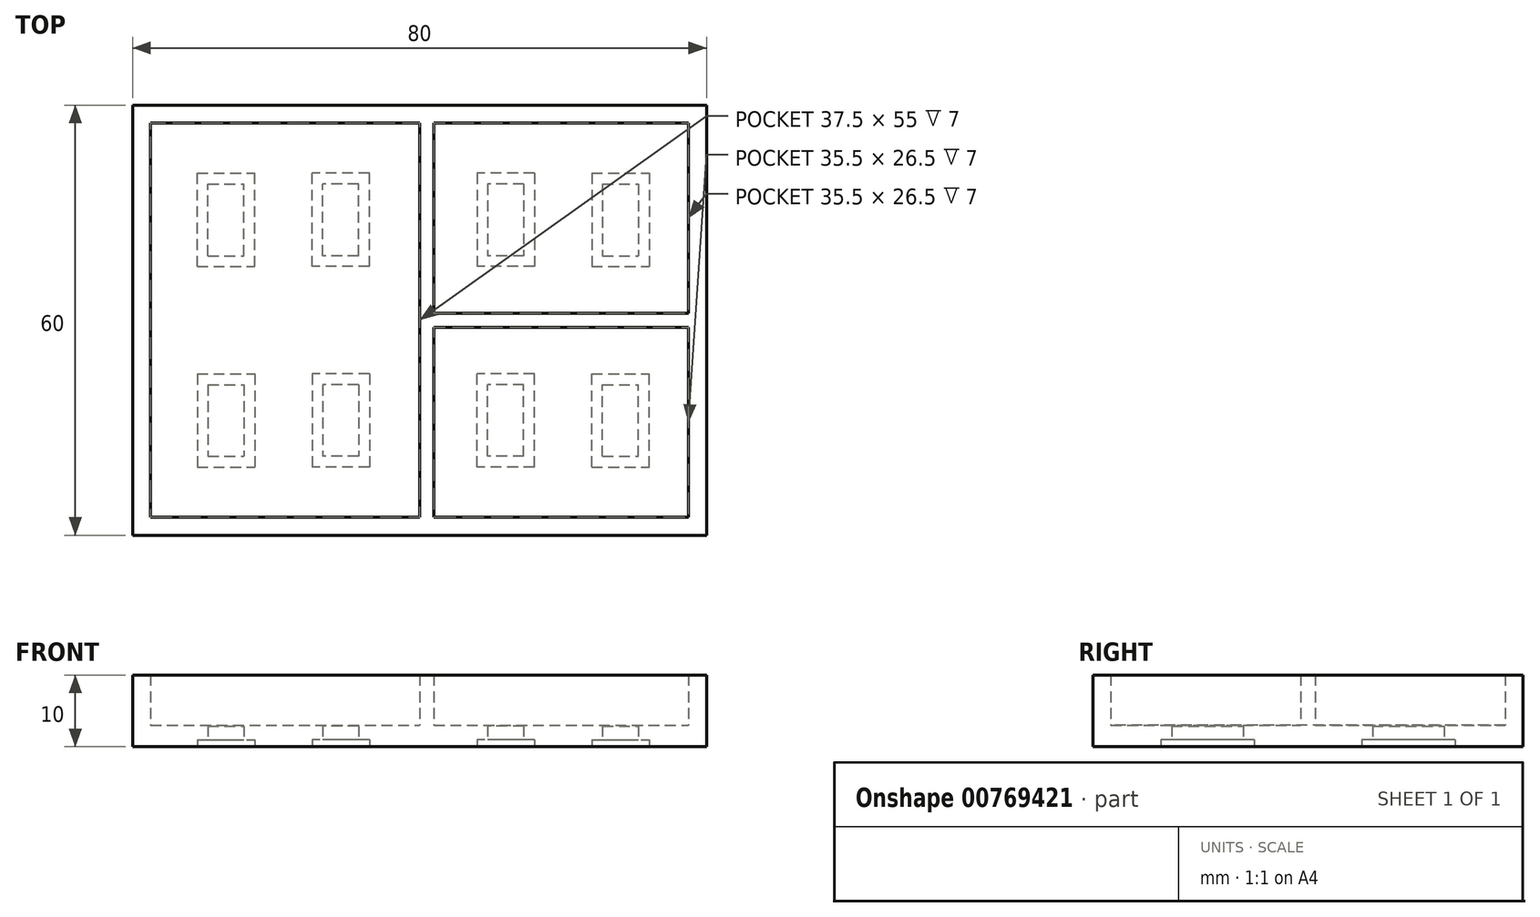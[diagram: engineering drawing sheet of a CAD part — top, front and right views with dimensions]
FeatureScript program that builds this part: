
annotation { "Feature Type Name" : "Feature", "Feature Type Description" : "" }
export const myFeature = defineFeature(function(context is Context, id is Id, definition is map)
    precondition{}
    {
        {
            var Q0;
            Q0=qCreatedBy(makeId("Top.planeOp"),FACE);
            var sketch = newSketch(context, id + "F0", { "sketchPlane" : qUnion([Q0])});
            skLineSegment(sketch, "E0.bottom", {"start": v(0, 0) * mm, "end": v(80, 0) * mm});
            skLineSegment(sketch, "E0.top", {"start": v(0, 60) * mm, "end": v(80, 60) * mm});
            skLineSegment(sketch, "E0.left", {"start": v(0, 0) * mm, "end": v(0, 60) * mm});
            skLineSegment(sketch, "E0.right", {"start": v(80, 0) * mm, "end": v(80, 60) * mm});
            skLineSegment(sketch, "E1", {"start": v(40, 57.5) * mm, "end": v(40, 2.5) * mm});
            skLineSegment(sketch, "E2.0", {"start": v(42, 29) * mm, "end": v(77.5, 29) * mm});
            skLineSegment(sketch, "E3.0", {"start": v(42, 31) * mm, "end": v(77.5, 31) * mm});
            skPoint(sketch, "E4.orphan", {"position": v(80, 30) * mm});
            skPoint(sketch, "E5.start.orphan", {"position": v(40, 30) * mm});
            skLineSegment(sketch, "E6.0", {"start": v(2.5, 2.5) * mm, "end": v(2.5, 57.5) * mm});
            skLineSegment(sketch, "E6.1", {"start": v(2.5, 2.5) * mm, "end": v(40, 2.5) * mm});
            skLineSegment(sketch, "E6.2", {"start": v(77.5, 2.5) * mm, "end": v(77.5, 29) * mm});
            skLineSegment(sketch, "E6.3", {"start": v(2.5, 57.5) * mm, "end": v(40, 57.5) * mm});
            skLineSegment(sketch, "E7", {"start": v(42, 2.5) * mm, "end": v(42, 29) * mm});
            skLineSegment(sketch, "E8.trimOffspring", {"start": v(42, 31) * mm, "end": v(42, 57.5) * mm});
            skLineSegment(sketch, "E9.trimOffspring", {"start": v(77.5, 31) * mm, "end": v(77.5, 57.5) * mm});
            skLineSegment(sketch, "E10.trimOffspring", {"start": v(42, 2.5) * mm, "end": v(77.5, 2.5) * mm});
            skPoint(sketch, "E11.orphan", {"position": v(40, 0) * mm});
            skLineSegment(sketch, "E12.trimOffspring", {"start": v(42, 57.5) * mm, "end": v(77.5, 57.5) * mm});
            skPoint(sketch, "E13.orphan", {"position": v(40, 60) * mm});
            skLineSegment(sketch, "E14", {"start": v(21, 0) * mm, "end": v(21, 60) * mm, "construction": true});
            skLineSegment(sketch, "E15", {"start": v(0, 44) * mm, "end": v(80, 44) * mm, "construction": true});
            skLineSegment(sketch, "E16", {"start": v(0, 16) * mm, "end": v(80, 16) * mm, "construction": true});
            skLineSegment(sketch, "E17", {"start": v(60, 0) * mm, "end": v(60, 60) * mm, "construction": true});
            skPoint(sketch, "E18", {"position": v(13, 44) * mm});
            skLineSegment(sketch, "E19.bottom", {"start": v(10.5, 39) * mm, "end": v(15.5, 39) * mm});
            skLineSegment(sketch, "E19.top", {"start": v(10.5, 49) * mm, "end": v(15.5, 49) * mm});
            skLineSegment(sketch, "E19.left", {"start": v(10.5, 39) * mm, "end": v(10.5, 49) * mm});
            skLineSegment(sketch, "E19.right", {"start": v(15.5, 39) * mm, "end": v(15.5, 49) * mm});
            skLineSegment(sketch, "E20", {"start": v(40, 30) * mm, "end": v(2.5, 30) * mm});
            skLineSegment(sketch, "E21.MirrorCS", {"start": v(15.5, 21) * mm, "end": v(15.5, 11) * mm});
            skLineSegment(sketch, "E22.MirrorCS", {"start": v(10.5, 11) * mm, "end": v(15.5, 11) * mm});
            skLineSegment(sketch, "E23.MirrorCS", {"start": v(10.5, 21) * mm, "end": v(10.5, 11) * mm});
            skLineSegment(sketch, "E24.MirrorCS", {"start": v(10.5, 21) * mm, "end": v(15.5, 21) * mm});
            skLineSegment(sketch, "E25.MirrorCS", {"start": v(26.5, 39) * mm, "end": v(26.5, 49) * mm});
            skLineSegment(sketch, "E26.MirrorCS", {"start": v(31.5, 49) * mm, "end": v(26.5, 49) * mm});
            skLineSegment(sketch, "E27.MirrorCS", {"start": v(31.5, 39) * mm, "end": v(31.5, 49) * mm});
            skLineSegment(sketch, "E28.MirrorCS", {"start": v(31.5, 39) * mm, "end": v(26.5, 39) * mm});
            skLineSegment(sketch, "E29.MirrorCS", {"start": v(26.5, 21) * mm, "end": v(26.5, 11) * mm});
            skLineSegment(sketch, "E30.MirrorCS", {"start": v(31.5, 21) * mm, "end": v(26.5, 21) * mm});
            skLineSegment(sketch, "E31.MirrorCS", {"start": v(31.5, 21) * mm, "end": v(31.5, 11) * mm});
            skLineSegment(sketch, "E32.MirrorCS", {"start": v(31.5, 11) * mm, "end": v(26.5, 11) * mm});
            skPoint(sketch, "E33", {"position": v(52, 44) * mm});
            skLineSegment(sketch, "E34.bottom", {"start": v(54.5, 49) * mm, "end": v(49.5, 49) * mm});
            skLineSegment(sketch, "E34.top", {"start": v(54.5, 39) * mm, "end": v(49.5, 39) * mm});
            skLineSegment(sketch, "E34.left", {"start": v(54.5, 49) * mm, "end": v(54.5, 39) * mm});
            skLineSegment(sketch, "E34.right", {"start": v(49.5, 49) * mm, "end": v(49.5, 39) * mm});
            skLineSegment(sketch, "E35.MirrorCS", {"start": v(65.5, 49) * mm, "end": v(65.5, 39) * mm});
            skLineSegment(sketch, "E36.MirrorCS", {"start": v(65.5, 49) * mm, "end": v(70.5, 49) * mm});
            skLineSegment(sketch, "E37.MirrorCS", {"start": v(70.5, 49) * mm, "end": v(70.5, 39) * mm});
            skLineSegment(sketch, "E38.MirrorCS", {"start": v(65.5, 39) * mm, "end": v(70.5, 39) * mm});
            skLineSegment(sketch, "E39.MirrorCS", {"start": v(54.5, 21) * mm, "end": v(49.5, 21) * mm});
            skLineSegment(sketch, "E40.MirrorCS", {"start": v(54.5, 11) * mm, "end": v(54.5, 21) * mm});
            skLineSegment(sketch, "E41.MirrorCS", {"start": v(54.5, 11) * mm, "end": v(49.5, 11) * mm});
            skLineSegment(sketch, "E42.MirrorCS", {"start": v(49.5, 11) * mm, "end": v(49.5, 21) * mm});
            skLineSegment(sketch, "E43.MirrorCS", {"start": v(65.5, 21) * mm, "end": v(70.5, 21) * mm});
            skLineSegment(sketch, "E44.MirrorCS", {"start": v(70.5, 11) * mm, "end": v(70.5, 21) * mm});
            skLineSegment(sketch, "E45.MirrorCS", {"start": v(65.5, 11) * mm, "end": v(70.5, 11) * mm});
            skLineSegment(sketch, "E46.MirrorCS", {"start": v(65.5, 11) * mm, "end": v(65.5, 21) * mm});
            skLineSegment(sketch, "E47.0", {"start": v(9, 50.5) * mm, "end": v(17, 50.5) * mm});
            skLineSegment(sketch, "E47.1", {"start": v(9, 37.5) * mm, "end": v(9, 50.5) * mm});
            skLineSegment(sketch, "E47.2", {"start": v(9, 37.5) * mm, "end": v(17, 37.5) * mm});
            skLineSegment(sketch, "E47.3", {"start": v(17, 37.5) * mm, "end": v(17, 50.5) * mm});
            skLineSegment(sketch, "E48.MirrorCS", {"start": v(33, 50.5) * mm, "end": v(25, 50.5) * mm});
            skLineSegment(sketch, "E49.MirrorCS", {"start": v(25, 37.5) * mm, "end": v(25, 50.5) * mm});
            skLineSegment(sketch, "E50.MirrorCS", {"start": v(33, 37.5) * mm, "end": v(33, 50.5) * mm});
            skLineSegment(sketch, "E51.MirrorCS", {"start": v(33, 37.5) * mm, "end": v(25, 37.5) * mm});
            skLineSegment(sketch, "E52.MirrorCS", {"start": v(17, 22.5) * mm, "end": v(17, 9.5) * mm});
            skLineSegment(sketch, "E53.MirrorCS", {"start": v(9, 22.5) * mm, "end": v(9, 9.5) * mm});
            skLineSegment(sketch, "E54.MirrorCS", {"start": v(9, 22.5) * mm, "end": v(17, 22.5) * mm});
            skLineSegment(sketch, "E55.MirrorCS", {"start": v(9, 9.5) * mm, "end": v(17, 9.5) * mm});
            skLineSegment(sketch, "E56.MirrorCS", {"start": v(33, 9.5) * mm, "end": v(25, 9.5) * mm});
            skLineSegment(sketch, "E57.MirrorCS", {"start": v(25, 22.5) * mm, "end": v(25, 9.5) * mm});
            skLineSegment(sketch, "E58.MirrorCS", {"start": v(33, 22.5) * mm, "end": v(25, 22.5) * mm});
            skLineSegment(sketch, "E59.MirrorCS", {"start": v(33, 22.5) * mm, "end": v(33, 9.5) * mm});
            skLineSegment(sketch, "E60.0", {"start": v(48, 50.5) * mm, "end": v(48, 37.5) * mm});
            skLineSegment(sketch, "E60.1", {"start": v(56, 50.5) * mm, "end": v(48, 50.5) * mm});
            skLineSegment(sketch, "E60.2", {"start": v(56, 50.5) * mm, "end": v(56, 37.5) * mm});
            skLineSegment(sketch, "E60.3", {"start": v(56, 37.5) * mm, "end": v(48, 37.5) * mm});
            skLineSegment(sketch, "E61.MirrorCS", {"start": v(64, 50.5) * mm, "end": v(72, 50.5) * mm});
            skLineSegment(sketch, "E62.MirrorCS", {"start": v(64, 50.5) * mm, "end": v(64, 37.5) * mm});
            skLineSegment(sketch, "E63.MirrorCS", {"start": v(72, 50.5) * mm, "end": v(72, 37.5) * mm});
            skLineSegment(sketch, "E64.MirrorCS", {"start": v(64, 37.5) * mm, "end": v(72, 37.5) * mm});
            skLineSegment(sketch, "E65.MirrorCS", {"start": v(56, 22.5) * mm, "end": v(48, 22.5) * mm});
            skLineSegment(sketch, "E66.MirrorCS", {"start": v(56, 9.5) * mm, "end": v(56, 22.5) * mm});
            skLineSegment(sketch, "E67.MirrorCS", {"start": v(48, 9.5) * mm, "end": v(48, 22.5) * mm});
            skLineSegment(sketch, "E68.MirrorCS", {"start": v(56, 9.5) * mm, "end": v(48, 9.5) * mm});
            skLineSegment(sketch, "E69.MirrorCS", {"start": v(64, 9.5) * mm, "end": v(72, 9.5) * mm});
            skLineSegment(sketch, "E70.MirrorCS", {"start": v(64, 9.5) * mm, "end": v(64, 22.5) * mm});
            skLineSegment(sketch, "E71.MirrorCS", {"start": v(72, 9.5) * mm, "end": v(72, 22.5) * mm});
            skLineSegment(sketch, "E72.MirrorCS", {"start": v(64, 22.5) * mm, "end": v(72, 22.5) * mm});
            skLineSegment(sketch, "E73.trimOffspring", {"start": v(0, 30) * mm, "end": v(-30.47, 30) * mm});
            skSolve(sketch);
        }
        {
            var Q0;
            Q0=makeQuery(id+"F0.imprint","IMPRINT",FACE,{"disambiguationData":[TD([[makeQuery(id+"F0.imprint","IMPRINT",EDGE,{"derivedFrom":sQuery(id+"F0.wireOp",EDGE,"E0.bottom")}),1.0]])]});
            extrude(context, id + "F1", {"entities" : qUnion([Q0]), "depth" : 10 * mm, "offsetDistance" : 25 * mm});
        }
        {
            var Q0;
            Q0=makeQuery(id+"F0.imprint","IMPRINT",FACE,{"disambiguationData":[TD([[makeQuery(id+"F0.imprint","IMPRINT",EDGE,{"derivedFrom":sQuery(id+"F0.wireOp",EDGE,"E1")}),-1.0]])]});
            var Q1;
            Q1=makeQuery(id+"F0.imprint","IMPRINT",FACE,{"disambiguationData":[TD([[makeQuery(id+"F0.imprint","IMPRINT",EDGE,{"derivedFrom":sQuery(id+"F0.wireOp",EDGE,"E3.0")}),1.0]])]});
            var Q2;
            Q2=makeQuery(id+"F0.imprint","IMPRINT",FACE,{"disambiguationData":[TD([[makeQuery(id+"F0.imprint","IMPRINT",EDGE,{"derivedFrom":sQuery(id+"F0.wireOp",EDGE,"E2.0")}),-1.0]])]});
            var Q3;
            Q3=makeQuery(id+"F0.imprint","IMPRINT",FACE,{"disambiguationData":[TD([[makeQuery(id+"F0.imprint","IMPRINT",EDGE,{"derivedFrom":sQuery(id+"F0.wireOp",EDGE,"E19.bottom")}),1.0]])]});
            var Q4;
            Q4=makeQuery(id+"F0.imprint","IMPRINT",FACE,{"disambiguationData":[TD([[makeQuery(id+"F0.imprint","IMPRINT",EDGE,{"derivedFrom":sQuery(id+"F0.wireOp",EDGE,"E19.bottom")}),-1.0]])]});
            var Q5;
            Q5=makeQuery(id+"F0.imprint","IMPRINT",FACE,{"disambiguationData":[TD([[makeQuery(id+"F0.imprint","IMPRINT",EDGE,{"derivedFrom":sQuery(id+"F0.wireOp",EDGE,"E25.MirrorCS")}),-1.0]])]});
            var Q6;
            Q6=makeQuery(id+"F0.imprint","IMPRINT",FACE,{"disambiguationData":[TD([[makeQuery(id+"F0.imprint","IMPRINT",EDGE,{"derivedFrom":sQuery(id+"F0.wireOp",EDGE,"E25.MirrorCS")}),1.0]])]});
            var Q7;
            Q7=makeQuery(id+"F0.imprint","IMPRINT",FACE,{"disambiguationData":[TD([[makeQuery(id+"F0.imprint","IMPRINT",EDGE,{"derivedFrom":sQuery(id+"F0.wireOp",EDGE,"E34.bottom")}),1.0]])]});
            var Q8;
            Q8=makeQuery(id+"F0.imprint","IMPRINT",FACE,{"disambiguationData":[TD([[makeQuery(id+"F0.imprint","IMPRINT",EDGE,{"derivedFrom":sQuery(id+"F0.wireOp",EDGE,"E34.bottom")}),-1.0]])]});
            var Q9;
            Q9=makeQuery(id+"F0.imprint","IMPRINT",FACE,{"disambiguationData":[TD([[makeQuery(id+"F0.imprint","IMPRINT",EDGE,{"derivedFrom":sQuery(id+"F0.wireOp",EDGE,"E35.MirrorCS")}),1.0]])]});
            var Q10;
            Q10=makeQuery(id+"F0.imprint","IMPRINT",FACE,{"disambiguationData":[TD([[makeQuery(id+"F0.imprint","IMPRINT",EDGE,{"derivedFrom":sQuery(id+"F0.wireOp",EDGE,"E35.MirrorCS")}),-1.0]])]});
            var Q11;
            Q11=makeQuery(id+"F0.imprint","IMPRINT",FACE,{"disambiguationData":[TD([[makeQuery(id+"F0.imprint","IMPRINT",EDGE,{"derivedFrom":sQuery(id+"F0.wireOp",EDGE,"E43.MirrorCS")}),-1.0]])]});
            var Q12;
            Q12=makeQuery(id+"F0.imprint","IMPRINT",FACE,{"disambiguationData":[TD([[makeQuery(id+"F0.imprint","IMPRINT",EDGE,{"derivedFrom":sQuery(id+"F0.wireOp",EDGE,"E43.MirrorCS")}),1.0]])]});
            var Q13;
            Q13=makeQuery(id+"F0.imprint","IMPRINT",FACE,{"disambiguationData":[TD([[makeQuery(id+"F0.imprint","IMPRINT",EDGE,{"derivedFrom":sQuery(id+"F0.wireOp",EDGE,"E39.MirrorCS")}),1.0]])]});
            var Q14;
            Q14=makeQuery(id+"F0.imprint","IMPRINT",FACE,{"disambiguationData":[TD([[makeQuery(id+"F0.imprint","IMPRINT",EDGE,{"derivedFrom":sQuery(id+"F0.wireOp",EDGE,"E39.MirrorCS")}),-1.0]])]});
            var Q15;
            Q15=makeQuery(id+"F0.imprint","IMPRINT",FACE,{"disambiguationData":[TD([[makeQuery(id+"F0.imprint","IMPRINT",EDGE,{"derivedFrom":sQuery(id+"F0.wireOp",EDGE,"E29.MirrorCS")}),1.0]])]});
            var Q16;
            Q16=makeQuery(id+"F0.imprint","IMPRINT",FACE,{"disambiguationData":[TD([[makeQuery(id+"F0.imprint","IMPRINT",EDGE,{"derivedFrom":sQuery(id+"F0.wireOp",EDGE,"E29.MirrorCS")}),-1.0]])]});
            var Q17;
            Q17=makeQuery(id+"F0.imprint","IMPRINT",FACE,{"disambiguationData":[TD([[makeQuery(id+"F0.imprint","IMPRINT",EDGE,{"derivedFrom":sQuery(id+"F0.wireOp",EDGE,"E21.MirrorCS")}),-1.0]])]});
            var Q18;
            Q18=makeQuery(id+"F0.imprint","IMPRINT",FACE,{"disambiguationData":[TD([[makeQuery(id+"F0.imprint","IMPRINT",EDGE,{"derivedFrom":sQuery(id+"F0.wireOp",EDGE,"E21.MirrorCS")}),1.0]])]});
            extrude(context, id + "F2", {"entities" : qUnion([Q0, Q1, Q2, Q3, Q4, Q5, Q6, Q7, Q8, Q9, Q10, Q11, Q12, Q13, Q14, Q15, Q16, Q17, Q18]), "operationType" : NewBodyOperationType.ADD, "depth" : 3 * mm, "offsetDistance" : 25 * mm});
        }
        {
            var Q0;
            Q0=makeQuery(id+"F0.imprint","IMPRINT",FACE,{"disambiguationData":[TD([[makeQuery(id+"F0.imprint","IMPRINT",EDGE,{"derivedFrom":sQuery(id+"F0.wireOp",EDGE,"E35.MirrorCS")}),-1.0]])]});
            var Q1;
            Q1=makeQuery(id+"F0.imprint","IMPRINT",FACE,{"disambiguationData":[TD([[makeQuery(id+"F0.imprint","IMPRINT",EDGE,{"derivedFrom":sQuery(id+"F0.wireOp",EDGE,"E34.bottom")}),-1.0]])]});
            var Q2;
            Q2=makeQuery(id+"F0.imprint","IMPRINT",FACE,{"disambiguationData":[TD([[makeQuery(id+"F0.imprint","IMPRINT",EDGE,{"derivedFrom":sQuery(id+"F0.wireOp",EDGE,"E39.MirrorCS")}),-1.0]])]});
            var Q3;
            Q3=makeQuery(id+"F0.imprint","IMPRINT",FACE,{"disambiguationData":[TD([[makeQuery(id+"F0.imprint","IMPRINT",EDGE,{"derivedFrom":sQuery(id+"F0.wireOp",EDGE,"E43.MirrorCS")}),1.0]])]});
            var Q4;
            Q4=makeQuery(id+"F0.imprint","IMPRINT",FACE,{"disambiguationData":[TD([[makeQuery(id+"F0.imprint","IMPRINT",EDGE,{"derivedFrom":sQuery(id+"F0.wireOp",EDGE,"E25.MirrorCS")}),1.0]])]});
            var Q5;
            Q5=makeQuery(id+"F0.imprint","IMPRINT",FACE,{"disambiguationData":[TD([[makeQuery(id+"F0.imprint","IMPRINT",EDGE,{"derivedFrom":sQuery(id+"F0.wireOp",EDGE,"E19.bottom")}),-1.0]])]});
            var Q6;
            Q6=makeQuery(id+"F0.imprint","IMPRINT",FACE,{"disambiguationData":[TD([[makeQuery(id+"F0.imprint","IMPRINT",EDGE,{"derivedFrom":sQuery(id+"F0.wireOp",EDGE,"E21.MirrorCS")}),1.0]])]});
            var Q7;
            Q7=makeQuery(id+"F0.imprint","IMPRINT",FACE,{"disambiguationData":[TD([[makeQuery(id+"F0.imprint","IMPRINT",EDGE,{"derivedFrom":sQuery(id+"F0.wireOp",EDGE,"E29.MirrorCS")}),-1.0]])]});
            extrude(context, id + "F3", {"entities" : qUnion([Q0, Q1, Q2, Q3, Q4, Q5, Q6, Q7]), "operationType" : NewBodyOperationType.REMOVE, "depth" : 1 * mm, "offsetDistance" : 25 * mm});
        }
        {
            var Q0;
            Q0=makeQuery(id+"F0.imprint","IMPRINT",FACE,{"disambiguationData":[TD([[makeQuery(id+"F0.imprint","IMPRINT",EDGE,{"derivedFrom":sQuery(id+"F0.wireOp",EDGE,"E35.MirrorCS")}),1.0]])]});
            var Q1;
            Q1=makeQuery(id+"F0.imprint","IMPRINT",FACE,{"disambiguationData":[TD([[makeQuery(id+"F0.imprint","IMPRINT",EDGE,{"derivedFrom":sQuery(id+"F0.wireOp",EDGE,"E34.bottom")}),1.0]])]});
            var Q2;
            Q2=makeQuery(id+"F0.imprint","IMPRINT",FACE,{"disambiguationData":[TD([[makeQuery(id+"F0.imprint","IMPRINT",EDGE,{"derivedFrom":sQuery(id+"F0.wireOp",EDGE,"E25.MirrorCS")}),-1.0]])]});
            var Q3;
            Q3=makeQuery(id+"F0.imprint","IMPRINT",FACE,{"disambiguationData":[TD([[makeQuery(id+"F0.imprint","IMPRINT",EDGE,{"derivedFrom":sQuery(id+"F0.wireOp",EDGE,"E19.bottom")}),1.0]])]});
            var Q4;
            Q4=makeQuery(id+"F0.imprint","IMPRINT",FACE,{"disambiguationData":[TD([[makeQuery(id+"F0.imprint","IMPRINT",EDGE,{"derivedFrom":sQuery(id+"F0.wireOp",EDGE,"E21.MirrorCS")}),-1.0]])]});
            var Q5;
            Q5=makeQuery(id+"F0.imprint","IMPRINT",FACE,{"disambiguationData":[TD([[makeQuery(id+"F0.imprint","IMPRINT",EDGE,{"derivedFrom":sQuery(id+"F0.wireOp",EDGE,"E29.MirrorCS")}),1.0]])]});
            var Q6;
            Q6=makeQuery(id+"F0.imprint","IMPRINT",FACE,{"disambiguationData":[TD([[makeQuery(id+"F0.imprint","IMPRINT",EDGE,{"derivedFrom":sQuery(id+"F0.wireOp",EDGE,"E39.MirrorCS")}),1.0]])]});
            var Q7;
            Q7=makeQuery(id+"F0.imprint","IMPRINT",FACE,{"disambiguationData":[TD([[makeQuery(id+"F0.imprint","IMPRINT",EDGE,{"derivedFrom":sQuery(id+"F0.wireOp",EDGE,"E43.MirrorCS")}),-1.0]])]});
            extrude(context, id + "F4", {"entities" : qUnion([Q0, Q1, Q2, Q3, Q4, Q5, Q6, Q7]), "operationType" : NewBodyOperationType.REMOVE, "depth" : 2.9 * mm, "offsetDistance" : 25 * mm});
        }
    });
